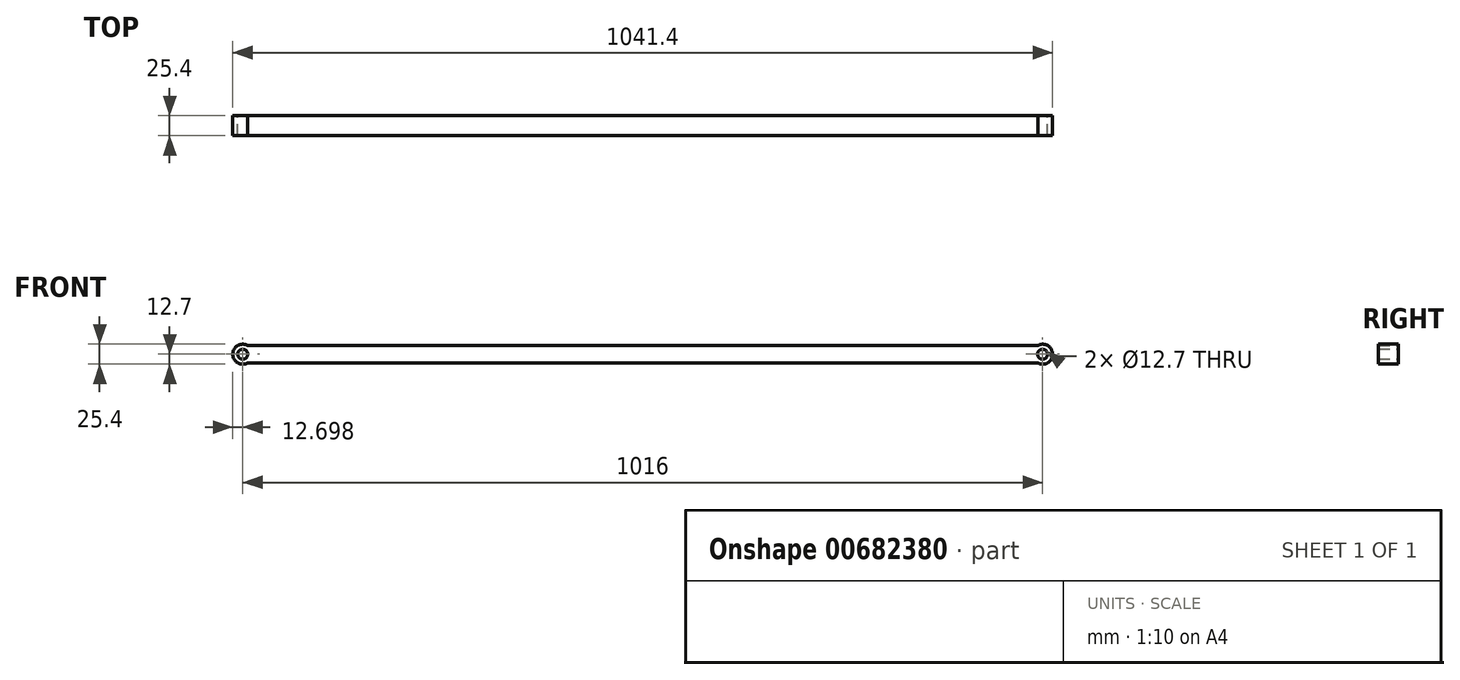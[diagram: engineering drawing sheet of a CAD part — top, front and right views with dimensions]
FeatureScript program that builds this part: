
annotation { "Feature Type Name" : "Feature", "Feature Type Description" : "" }
export const myFeature = defineFeature(function(context is Context, id is Id, definition is map)
    precondition{}
    {
        {
            var Q0;
            Q0=qCreatedBy(makeId("Front.planeOp"),FACE);
            var sketch = newSketch(context, id + "F0", { "sketchPlane" : qUnion([Q0])});
            skCircle(sketch, "E0", {"center": v(-36.8, 0) * mm, "radius": 6.35 * mm});
            skLineSegment(sketch, "E1", {"start": v(-36.8, 0) * mm, "end": v(979.2, 0) * mm, "construction": true});
            skCircle(sketch, "E2", {"center": v(979.2, 0) * mm, "radius": 6.35 * mm});
            skArc(sketch, "E3", {"start": v(973.33, -11.26) * mm, "mid": v(991.9, 0) * mm, "end": v(973.33, 11.26) * mm});
            skArc(sketch, "E4", {"start": v(-30.93, 11.26) * mm, "mid": v(-49.5, 0) * mm, "end": v(-30.93, -11.26) * mm});
            skLineSegment(sketch, "E5", {"start": v(-30.93, 11.26) * mm, "end": v(973.33, 11.26) * mm});
            skLineSegment(sketch, "E6.MirrorCS", {"start": v(-30.93, -11.26) * mm, "end": v(973.33, -11.26) * mm});
            skSolve(sketch);
        }
        {
            var Q0;
            Q0=makeQuery(id+"F0.imprint","IMPRINT",FACE,{"disambiguationData":[TD([[makeQuery(id+"F0.imprint","IMPRINT",EDGE,{"derivedFrom":sQuery(id+"F0.wireOp",EDGE,"E0")}),-1.0]])]});
            extrude(context, id + "F1", {"entities" : qUnion([Q0]), "depth" : 25.4 * mm, "offsetDistance" : 25.4 * mm});
        }
    });
